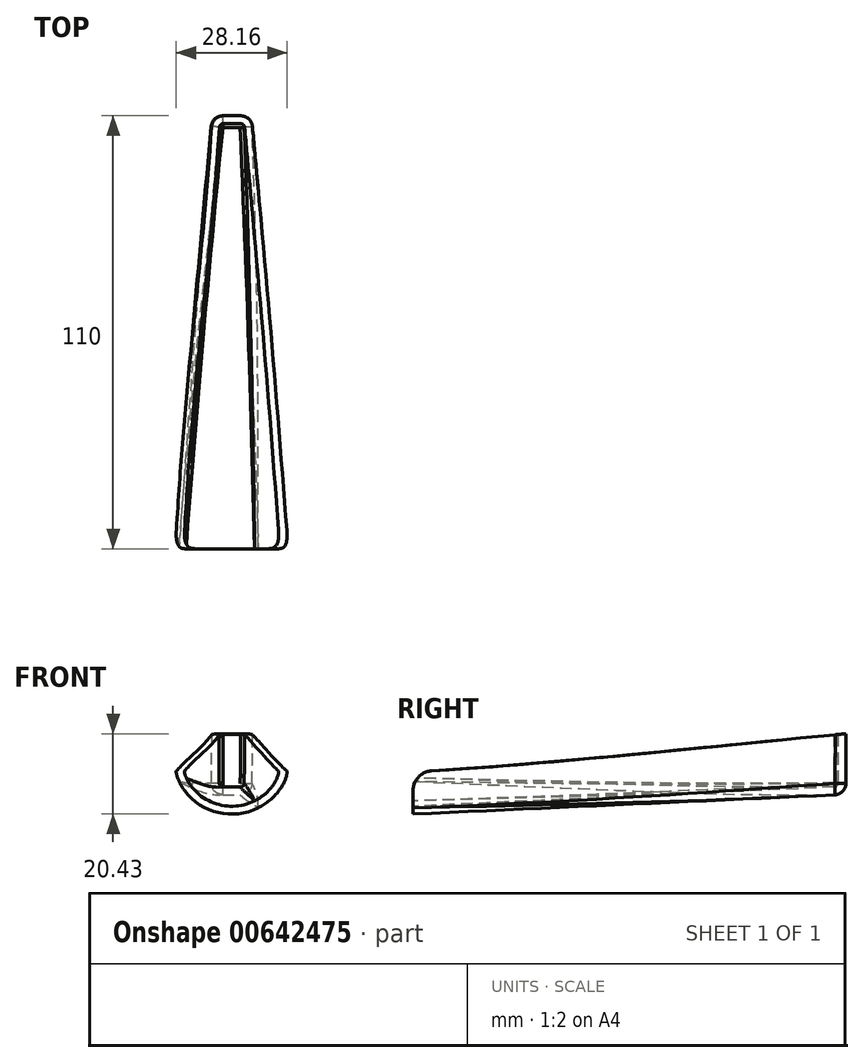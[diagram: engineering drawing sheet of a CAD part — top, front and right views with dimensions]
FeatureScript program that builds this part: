
annotation { "Feature Type Name" : "Feature", "Feature Type Description" : "" }
export const myFeature = defineFeature(function(context is Context, id is Id, definition is map)
    precondition{}
    {
        {
            var Q0;
            Q0=qCreatedBy(makeId("Front.planeOp"),FACE);
            var sketch = newSketch(context, id + "F0", { "sketchPlane" : qUnion([Q0])});
            skLineSegment(sketch, "E0.bottom", {"start": v(5, -10) * mm, "end": v(-5, -10) * mm});
            skLineSegment(sketch, "E0.top", {"start": v(5, 10) * mm, "end": v(-5, 10) * mm});
            skLineSegment(sketch, "E0.left", {"start": v(5, -10) * mm, "end": v(5, 10) * mm});
            skLineSegment(sketch, "E0.right", {"start": v(-5, -10) * mm, "end": v(-5, 10) * mm});
            skPoint(sketch, "E0.middle", {"position": v(0, 0) * mm});
            skSolve(sketch);
        }
        {
            var Q0;
            Q0=qCreatedBy(makeId("Front.planeOp"),FACE);
            cPlane(context, id + "F1", {"entities" : qUnion([Q0]), "cplaneType" : CPlaneType.OFFSET, "offset" : 110 * mm, "width" : 150 * mm, "height" : 150 * mm});
        }
        {
            var Q0;
            Q0=qCreatedBy(id+"F1.planeOp",FACE);
            var sketch = newSketch(context, id + "F2", { "sketchPlane" : qUnion([Q0])});
            skCircle(sketch, "E1", {"center": v(0, 0) * mm, "radius": 15 * mm});
            skSolve(sketch);
        }
        {
            var Q0;
            Q0=makeQuery(id+"F0.imprint","IMPRINT",FACE,{"disambiguationData":[TD([[makeQuery(id+"F0.imprint","IMPRINT",EDGE,{"derivedFrom":sQuery(id+"F0.wireOp",EDGE,"E0.bottom")}),-1.0]])]});
            var Q1;
            Q1=makeQuery(id+"F2.imprint","IMPRINT",FACE,{"disambiguationData":[TD([[makeQuery(id+"F2.imprint","IMPRINT",EDGE,{"derivedFrom":sQuery(id+"F2.wireOp",EDGE,"E1")}),1.0]])]});
            loft(context, id + "F3", {"sheetProfilesArray" : [{ "sheetProfileEntities" : qUnion([Q0]) }, { "sheetProfileEntities" : qUnion([Q1]) }]});
        }
        {
            var Q0;
            Q0=makeQuery(id+"F3.opLoft","MID_CAP_EDGE",EDGE,{"disambiguationData":[OSD([sQuery(id+"F0.wireOp",EDGE,"E0.bottom"),sQuery(id+"F0.wireOp",EDGE,"E0.top"),sQuery(id+"F0.wireOp",EDGE,"E0.right")])],"capPos":0.0});
            var Q1;
            Q1=makeQuery(id+"F3.opLoft","MID_CAP_EDGE",EDGE,{"disambiguationData":[OSD([sQuery(id+"F0.wireOp",EDGE,"E0.bottom"),sQuery(id+"F0.wireOp",EDGE,"E0.top"),sQuery(id+"F0.wireOp",EDGE,"E0.left")])],"capPos":0.0});
            var Q2;
            Q2=makeQuery(id+"F3.opLoft","MID_CAP_EDGE",EDGE,{"disambiguationData":[OSD([sQuery(id+"F0.wireOp",EDGE,"E0.top"),sQuery(id+"F0.wireOp",EDGE,"E0.left"),sQuery(id+"F0.wireOp",EDGE,"E0.right")])],"capPos":0.0});
            var Q3;
            Q3=makeQuery(id+"F3.opLoft","SWEPT_EDGE",EDGE,{"disambiguationData":[OSD([sQuery(id+"F0.wireOp",EDGE,"E0.bottom"),sQuery(id+"F0.wireOp",EDGE,"E0.top"),sQuery(id+"F0.wireOp",EDGE,"E0.right"),sQuery(id+"F2.wireOp",EDGE,"E1")])]});
            var Q4;
            Q4=makeQuery(id+"F3.opLoft","SWEPT_EDGE",EDGE,{"disambiguationData":[OSD([sQuery(id+"F0.wireOp",EDGE,"E0.bottom"),sQuery(id+"F0.wireOp",EDGE,"E0.left")])]});
            var Q5;
            Q5=makeQuery(id+"F3.opLoft","MID_CAP_EDGE",EDGE,{"disambiguationData":[OSD([sQuery(id+"F0.wireOp",EDGE,"E0.bottom"),sQuery(id+"F0.wireOp",EDGE,"E0.left"),sQuery(id+"F0.wireOp",EDGE,"E0.right")])],"capPos":0.0});
            var Q6;
            Q6=makeQuery(id+"F3.opLoft","SWEPT_EDGE",EDGE,{"disambiguationData":[OSD([sQuery(id+"F0.wireOp",EDGE,"E0.bottom"),sQuery(id+"F0.wireOp",EDGE,"E0.top"),sQuery(id+"F0.wireOp",EDGE,"E0.left"),sQuery(id+"F2.wireOp",EDGE,"E1")])]});
            var Q7;
            Q7=makeQuery(id+"F3.opLoft","SWEPT_EDGE",EDGE,{"disambiguationData":[OSD([sQuery(id+"F0.wireOp",EDGE,"E0.top"),sQuery(id+"F0.wireOp",EDGE,"E0.left"),sQuery(id+"F0.wireOp",EDGE,"E0.right"),sQuery(id+"F2.wireOp",EDGE,"E1")])]});
            fillet(context, id + "F4", {"entities" : qUnion([Q0, Q1, Q2, Q3, Q4, Q5, Q6, Q7]), "radius" : 3 * mm, "tangentPropagation" : true, "allowEdgeOverflow" : false});
        }
        {
            var Q0;
            Q0=makeQuery(id+"F3.opLoft","CAP_FACE",FACE,{"disambiguationData":[OSD([makeQuery(id+"F2.imprint","IMPRINT",FACE,{"disambiguationData":[TD([[makeQuery(id+"F2.imprint","IMPRINT",EDGE,{"derivedFrom":sQuery(id+"F2.wireOp",EDGE,"E1")}),1.0]])]})])],"isStart":true});
            shell(context, id + "F5", {"entities" : qUnion([Q0]), "thickness" : 2 * mm});
        }
        {
            var Q0;
            Q0=qCreatedBy(makeId("Right.planeOp"),FACE);
            var sketch = newSketch(context, id + "F6", { "sketchPlane" : qUnion([Q0])});
            skFitSpline(sketch, "E2", {"points": [v(-169.18, 0) * mm, v(20.6, 7.04) * mm, v(36.62, 9.7) * mm, v(-63.6, 52.42) * mm, v(-131.8, 35.43) * mm, v(-169.18, 0) * mm]});
            skSolve(sketch);
        }
        {
            var Q0;
            Q0=makeQuery(id+"F6.imprint","IMPRINT",FACE,{"disambiguationData":[TD([[makeQuery(id+"F6.imprint","IMPRINT",EDGE,{"derivedFrom":sQuery(id+"F6.wireOp",EDGE,"E2")}),1.0]])]});
            extrude(context, id + "F7", {"entities" : qUnion([Q0]), "operationType" : NewBodyOperationType.REMOVE, "endBound" : BoundingType.SYMMETRIC, "oppositeDirection" : true, "depth" : 44.4 * mm, "offsetDistance" : 25 * mm});
        }
        {
            var Q0;
            Q0=makeQuery(id+"F7.boolean.opBoolean","INTERSECT",EDGE,{"disambiguationData":[OD(0.0)],"derivedFrom":[makeQuery(id+"F3.opLoft","CAP_FACE",FACE,{"disambiguationData":[OSD([makeQuery(id+"F2.imprint","IMPRINT",FACE,{"disambiguationData":[TD([[makeQuery(id+"F2.imprint","IMPRINT",EDGE,{"derivedFrom":sQuery(id+"F2.wireOp",EDGE,"E1")}),1.0]])]})])],"isStart":true}),makeQuery(id+"F7.opExtrude","SWEPT_FACE",FACE,{"disambiguationData":[OSD([sQuery(id+"F6.wireOp",EDGE,"E2")])]})]});
            var Q1;
            Q1=makeQuery(id+"F7.boolean.opBoolean","INTERSECT",EDGE,{"disambiguationData":[OD(1.0)],"derivedFrom":[makeQuery(id+"F3.opLoft","CAP_FACE",FACE,{"disambiguationData":[OSD([makeQuery(id+"F2.imprint","IMPRINT",FACE,{"disambiguationData":[TD([[makeQuery(id+"F2.imprint","IMPRINT",EDGE,{"derivedFrom":sQuery(id+"F2.wireOp",EDGE,"E1")}),1.0]])]})])],"isStart":true}),makeQuery(id+"F7.opExtrude","SWEPT_FACE",FACE,{"disambiguationData":[OSD([sQuery(id+"F6.wireOp",EDGE,"E2")])]})]});
            fillet(context, id + "F8", {"entities" : qUnion([Q0, Q1]), "radius" : 5 * mm, "tangentPropagation" : true, "allowEdgeOverflow" : false});
        }
    });
